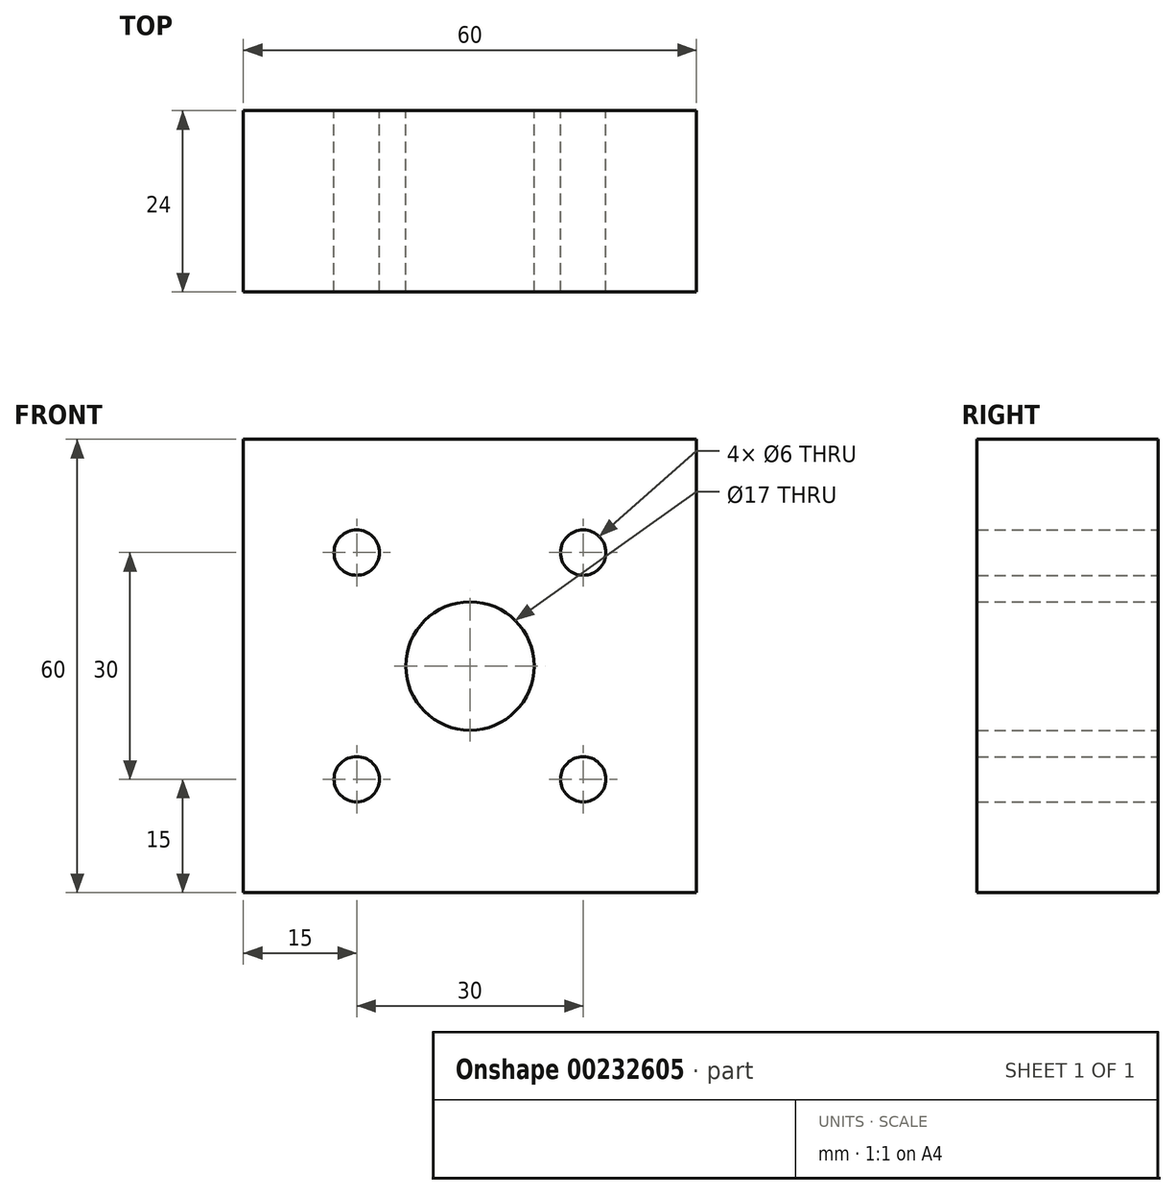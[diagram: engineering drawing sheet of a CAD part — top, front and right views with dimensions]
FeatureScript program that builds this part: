
annotation { "Feature Type Name" : "Feature", "Feature Type Description" : "" }
export const myFeature = defineFeature(function(context is Context, id is Id, definition is map)
    precondition{}
    {
        {
            var Q0;
            Q0=qCreatedBy(makeId("Front.planeOp"),FACE);
            var sketch = newSketch(context, id + "F0", { "sketchPlane" : qUnion([Q0])});
            skLineSegment(sketch, "E0.bottom", {"start": v(0, 0) * mm, "end": v(60, 0) * mm});
            skLineSegment(sketch, "E0.top", {"start": v(0, 60) * mm, "end": v(60, 60) * mm});
            skLineSegment(sketch, "E0.left", {"start": v(0, 0) * mm, "end": v(0, 60) * mm});
            skLineSegment(sketch, "E0.right", {"start": v(60, 0) * mm, "end": v(60, 60) * mm});
            skCircle(sketch, "E1", {"center": v(30, 30) * mm, "radius": 8.5 * mm});
            skCircle(sketch, "E2", {"center": v(15, 45) * mm, "radius": 3 * mm});
            skCircle(sketch, "E3", {"center": v(45, 45) * mm, "radius": 3 * mm});
            skCircle(sketch, "E4", {"center": v(15, 15) * mm, "radius": 3 * mm});
            skCircle(sketch, "E5", {"center": v(45, 15) * mm, "radius": 3 * mm});
            skSolve(sketch);
        }
        {
            var Q0;
            Q0 = qSketchRegion(id + "F0", true);
            extrude(context, id + "F1", {"entities" : qUnion([Q0]), "depth" : 24 * mm});
        }
    });
